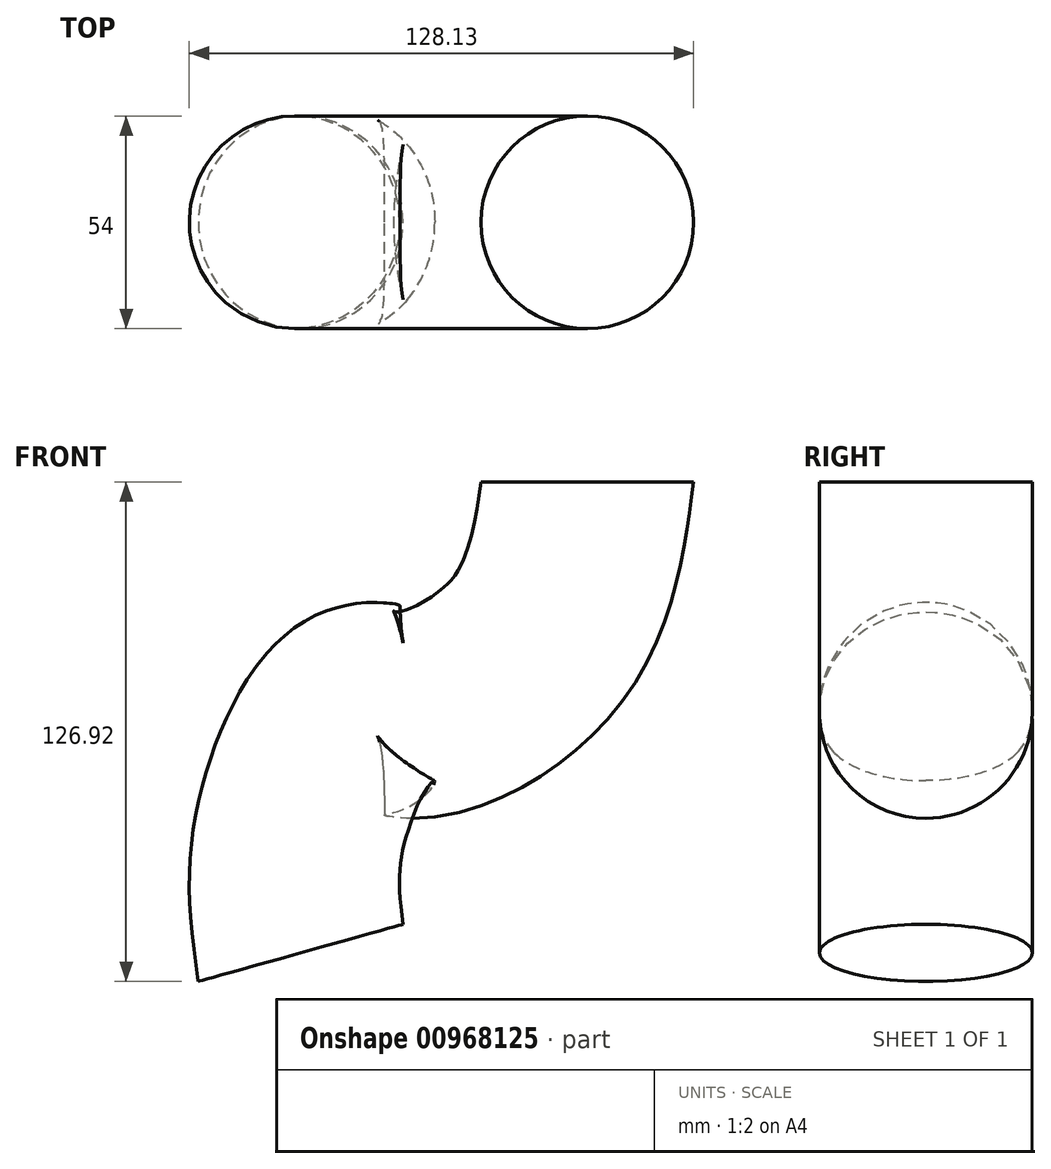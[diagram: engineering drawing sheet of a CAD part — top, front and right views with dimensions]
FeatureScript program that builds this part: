
annotation { "Feature Type Name" : "Feature", "Feature Type Description" : "" }
export const myFeature = defineFeature(function(context is Context, id is Id, definition is map)
    precondition{}
    {
        {
            var Q0;
            Q0=qCreatedBy(makeId("Top.planeOp"),FACE);
            var sketch = newSketch(context, id + "F0", { "sketchPlane" : qUnion([Q0])});
            skCircle(sketch, "E0", {"center": v(0, 0) * mm, "radius": 27 * mm});
            skSolve(sketch);
        }
        {
            var Q0;
            Q0=qCreatedBy(makeId("Front.planeOp"),FACE);
            var sketch = newSketch(context, id + "F1", { "sketchPlane" : qUnion([Q0])});
            skFitSpline(sketch, "E1", {"points": [v(0, 0) * mm, v(-12.52, -39.53) * mm, v(-43.28, -58.55) * mm, v(-57.67, -58.35) * mm, v(-73.01, -88.7) * mm, v(-72.85, -119.65) * mm], "startDerivative": vector(-26.19, -182.04) * mm, "endDerivative": vector(18.65, -143.03) * mm});
            skSolve(sketch);
        }
        {
            var Q0;
            Q0=makeQuery(id+"F0.imprint","IMPRINT",FACE,{"disambiguationData":[TD([[makeQuery(id+"F0.imprint","IMPRINT",EDGE,{"derivedFrom":sQuery(id+"F0.wireOp",EDGE,"E0")}),1.0]])]});
            var Q1;
            Q1 = qConstructionFilter(qBodyType(qCreatedBy(id + "F1" ,EDGE), BodyType.WIRE), ConstructionObject.NO);
            sweep(context, id + "F2", {"profiles" : qUnion([Q0]), "path" : qUnion([Q1])});
        }
    });
